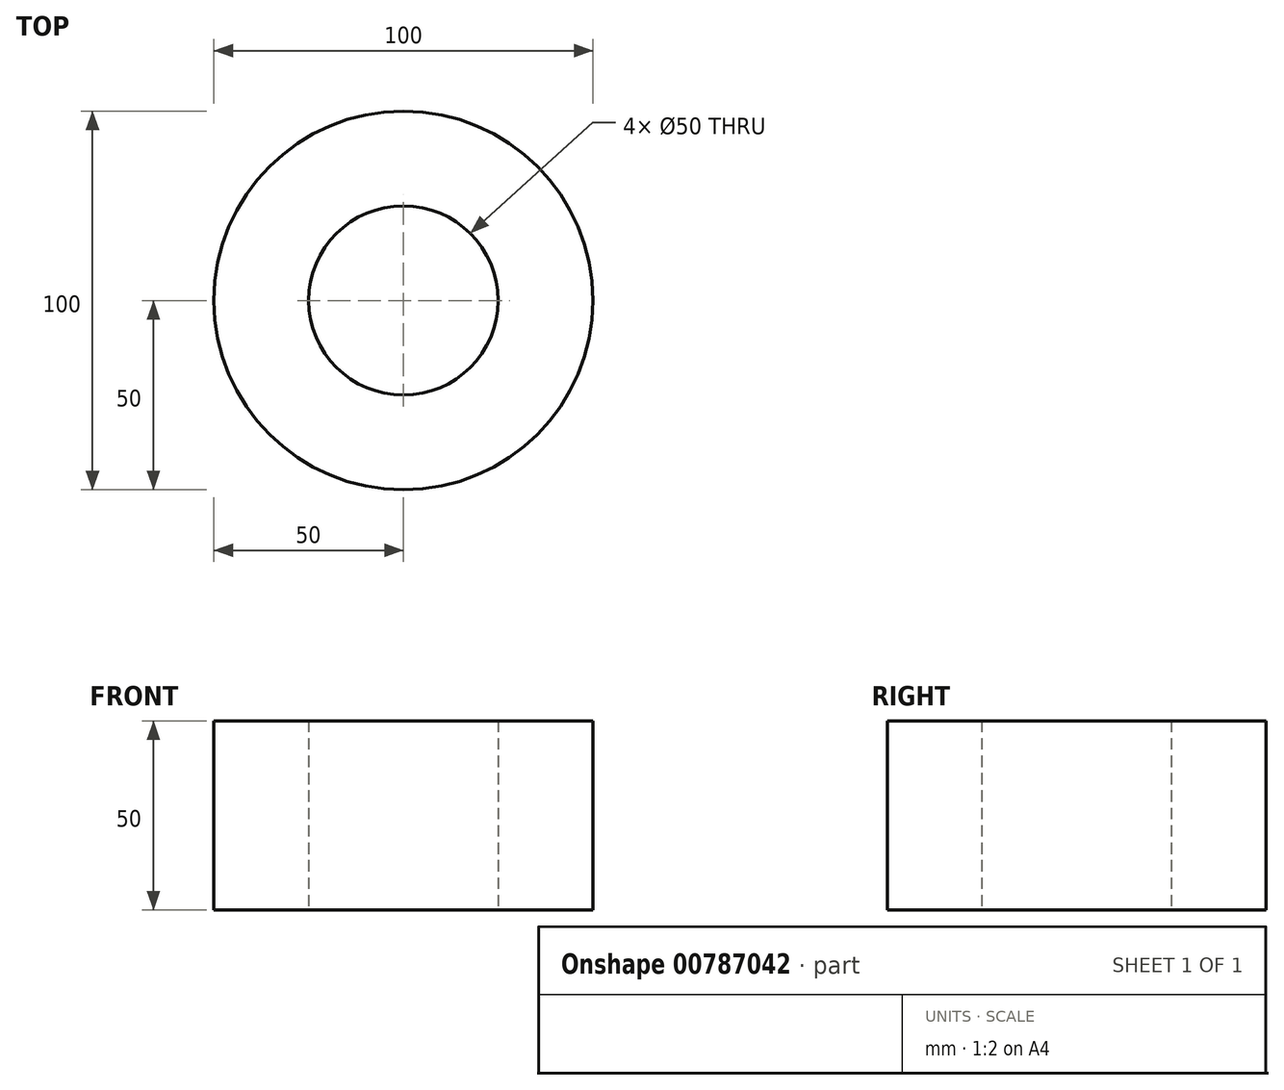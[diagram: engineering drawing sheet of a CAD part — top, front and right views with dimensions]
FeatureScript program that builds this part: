
annotation { "Feature Type Name" : "Feature", "Feature Type Description" : "" }
export const myFeature = defineFeature(function(context is Context, id is Id, definition is map)
    precondition{}
    {
        {
            var Q0;
            Q0=qCreatedBy(makeId("Top.planeOp"),FACE);
            var sketch = newSketch(context, id + "F0", { "sketchPlane" : qUnion([Q0])});
            skCircle(sketch, "E0", {"center": v(0, 0) * mm, "radius": 25 * mm});
            skCircle(sketch, "E1.0", {"center": v(0, 0) * mm, "radius": 50 * mm});
            skSolve(sketch);
        }
        {
            var Q0;
            Q0 = qSketchRegion(id + "F0", true);
            extrude(context, id + "F1", {"entities" : qUnion([Q0]), "depth" : 50 * mm, "offsetDistance" : 25 * mm});
        }
    });
